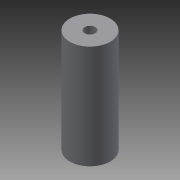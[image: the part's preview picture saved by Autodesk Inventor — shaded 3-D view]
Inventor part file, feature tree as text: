
AUTODESK INVENTOR PART (.ipt)
format: ipt  version: 2013 (Build 170138000, 138)  size: 72,192 bytes
history: native  units: mm
features: extrude x1, hole x1, sketch x1
ambient origin geometry x8: Origin, YZ Plane, XZ Plane, XY Plane, X Axis, Y Axis, Z Axis, Center Point
bodies: Solid1 (feature_tree)
feature tree (3):
  extrude  "Extrusion1"  Depth=30.0mm TaperAngle=0.0deg
  hole  "Hole1"  [1 undecoded]
  sketch  "Sketch1"  dims[d0=11.7mm d2=30.0mm d3=0.0mm d17=10.0mm d18=10.0mm d9=3.1mm d10=6.0mm d11=4.0mm d12=2.0mm d13=90.0deg d14=8.0mm d15=20.594885mm]
note: 1 required parameter value undecoded (feature->parameter linkage not recoverable at this tier; creation-order binding heuristic only, values carry confidence <= 0.55)
